# Revit family: Deca_V+ílvula de Escoamento_1602.C
name_source: partatom
category: Conexões hidráulicas
revit_build: Autodesk Revit 2013 (Build: 20120221_2030(x64)
units: mm (PartAtom-declared; Revit-internal decimal feet)

## types (3) — shared parameters
Aprovado por = Contino/quattroD
Atendimento ao Cliente = 0800-0117073
Consumo = Varia com a pressão
Criado por = Contino/quattroD
Código de montagem = D2020
Descrição = Válvula de escoamento para lavatório / cuba / bidê
Diâmetro Água Fria = 15  [stored 0.0492126 ft]
Fabricante = Deca
Flow Pressure = 0.00 psi
Informações Complementares = Não Aplicável
Linha = Válvula de escoamento
Louça/Metais = Metal
Material = Latão Cromado e Plástico de Engenharia
Norma = ABNT NBR 15423:2006
Peso Liquido (Kg) = 0.124
Pressão = 2 A 40 mca
Produto = Válvula de escoamento para lavatório / cuba / bidê
Raio Água Fria = 8  [stored 0.0262467 ft]
Segmento = Competitivo
URL = www.deca.com.br/produtos
Variações de COR = Cromado com tampão plástico (1602.C.PLA); Cromado (1602.C), Dourado (1602.D)
Vendido Separadamente = Não Aplicável
zero-valued in all types: CWFU, Elevação-padrão, WFU

## per-type parameters (varying)
| type | Código | Modelo | Válvula |
| 1602.C_Cromado CR10 | 1602.C | 1602.C | Deca CR10 Cromado Metal |
| 1602.D_Dourado | 1602.D | 1602.D | Deca GLD Gold Metal |
| 1602.C.PLA_Cromado com tampão plástico | 1602.C.PLA | 1602.C.PLA | Deca CR10 Cromado Metal |

note: [stored X ft] marks values corroborated as IEEE doubles in the binary element streams (Revit-internal decimal feet)

## geometry (parser evidence)
native form markers: Blend x10, Sweep x1
no freeform markers — native parametric forms only
